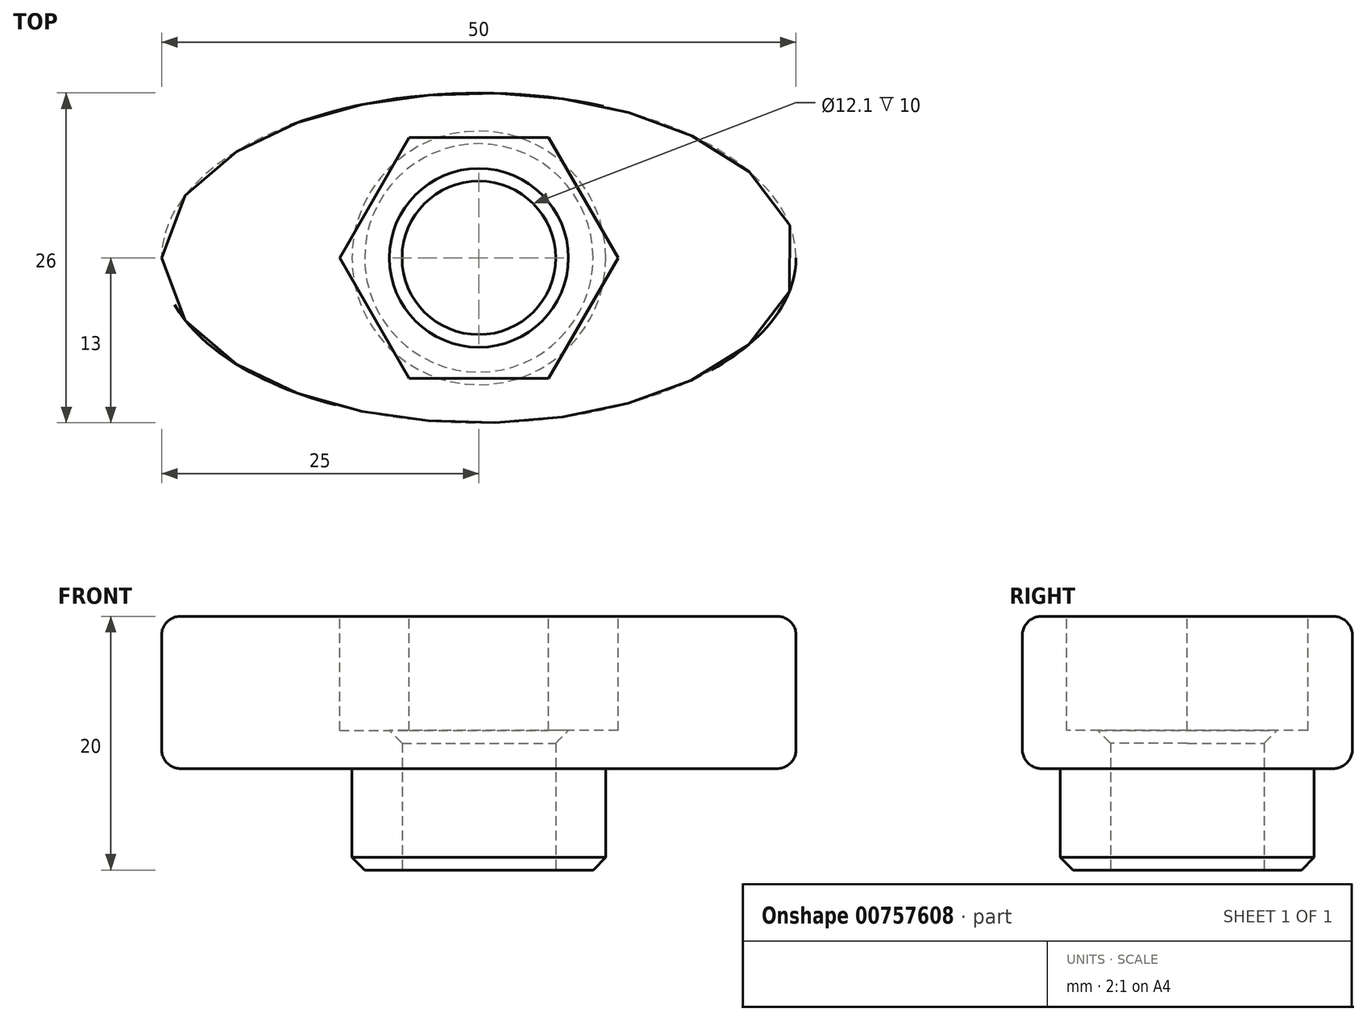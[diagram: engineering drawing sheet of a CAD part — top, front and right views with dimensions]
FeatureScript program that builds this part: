
annotation { "Feature Type Name" : "Feature", "Feature Type Description" : "" }
export const myFeature = defineFeature(function(context is Context, id is Id, definition is map)
    precondition{}
    {
        {
            var Q0;
            Q0=qCreatedBy(makeId("Top.planeOp"),FACE);
            var sketch = newSketch(context, id + "F0", { "sketchPlane" : qUnion([Q0])});
            skPoint(sketch, "E0", {"position": v(0, 13) * mm});
            skPoint(sketch, "E1", {"position": v(0, 0) * mm});
            skPoint(sketch, "E2", {"position": v(-25, 0) * mm});
            skEllipse(sketch, "E3", {"center": v(0, 0) * mm, "majorRadius": 25 * mm, "minorRadius": 13 * mm, "majorAxis": v(-1, 0)});
            skSolve(sketch);
        }
        {
            var Q0;
            Q0 = qSketchRegion(id + "F0", true);
            extrude(context, id + "F1", {"entities" : qUnion([Q0]), "depth" : 12 * mm, "offsetDistance" : 25 * mm});
        }
        {
            var Q0;
            Q0=makeQuery(id+"F1.opExtrude","CAP_FACE",FACE,{"disambiguationData":[OSD([sQuery(id+"F0.wireOp",EDGE,"E3")])],"isStart":true});
            var sketch = newSketch(context, id + "F2", { "sketchPlane" : qUnion([Q0])});
            skCircle(sketch, "E4", {"center": v(0, 0) * mm, "radius": 10 * mm});
            skSolve(sketch);
        }
        {
            var Q0;
            Q0 = qSketchRegion(id + "F2", true);
            extrude(context, id + "F3", {"entities" : qUnion([Q0]), "operationType" : NewBodyOperationType.ADD, "depth" : 8 * mm, "offsetDistance" : 25 * mm});
        }
        {
            var Q0;
            Q0=makeQuery(id+"F1.opExtrude","CAP_FACE",FACE,{"disambiguationData":[OSD([sQuery(id+"F0.wireOp",EDGE,"E3")])],"isStart":false});
            var sketch = newSketch(context, id + "F4", { "sketchPlane" : qUnion([Q0])});
            skCircle(sketch, "E5.cCircle", {"center": v(0, 0) * mm, "radius": 9.5 * mm, "construction": true});
            skLineSegment(sketch, "E5.0", {"start": v(10.97, 0) * mm, "end": v(5.48, -9.5) * mm});
            skLineSegment(sketch, "E5.1", {"start": v(5.48, -9.5) * mm, "end": v(-5.48, -9.5) * mm});
            skLineSegment(sketch, "E5.2", {"start": v(-5.48, -9.5) * mm, "end": v(-10.97, 0) * mm});
            skLineSegment(sketch, "E5.3", {"start": v(-10.97, 0) * mm, "end": v(-5.48, 9.5) * mm});
            skLineSegment(sketch, "E5.4", {"start": v(-5.48, 9.5) * mm, "end": v(5.48, 9.5) * mm});
            skLineSegment(sketch, "E5.5", {"start": v(5.48, 9.5) * mm, "end": v(10.97, 0) * mm});
            skPoint(sketch, "E5.0.midPoint", {"position": v(8.23, -4.75) * mm});
            skSolve(sketch);
        }
        {
            var Q0;
            Q0 = qSketchRegion(id + "F4", true);
            extrude(context, id + "F5", {"entities" : qUnion([Q0]), "operationType" : NewBodyOperationType.REMOVE, "oppositeDirection" : true, "depth" : 9 * mm, "offsetDistance" : 25 * mm});
        }
        {
            var Q0;
            Q0=makeQuery(id+"F3.opExtrude","CAP_FACE",FACE,{"disambiguationData":[OSD([sQuery(id+"F2.wireOp",EDGE,"E4")])],"isStart":false});
            var sketch = newSketch(context, id + "F6", { "sketchPlane" : qUnion([Q0])});
            skCircle(sketch, "E6", {"center": v(0, 0) * mm, "radius": 6.05 * mm});
            skSolve(sketch);
        }
        {
            var Q0;
            Q0 = qSketchRegion(id + "F6", true);
            extrude(context, id + "F7", {"entities" : qUnion([Q0]), "operationType" : NewBodyOperationType.REMOVE, "endBound" : BoundingType.THROUGH_ALL, "oppositeDirection" : true, "depth" : 25 * mm, "offsetDistance" : 25 * mm});
        }
        {
            var Q0;
            Q0=makeQuery(id+"F1.opExtrude","CAP_EDGE",EDGE,{"disambiguationData":[OSD([sQuery(id+"F0.wireOp",EDGE,"E3")])],"isStart":false});
            var Q1;
            Q1=makeQuery(id+"F1.opExtrude","CAP_EDGE",EDGE,{"disambiguationData":[OSD([sQuery(id+"F0.wireOp",EDGE,"E3")])],"isStart":true});
            var Q2;
            Q2=makeQuery(id+"F3.opExtrude","CAP_EDGE",EDGE,{"disambiguationData":[OSD([sQuery(id+"F2.wireOp",EDGE,"E4")])],"isStart":true});
            fillet(context, id + "F8", {"entities" : qUnion([Q0, Q1, Q2]), "radius" : 1.5 * mm, "tangentPropagation" : true, "allowEdgeOverflow" : false});
        }
        {
            var Q0;
            Q0=makeQuery(id+"F7.boolean.opBoolean","COPY",EDGE,{"derivedFrom":makeQuery(id+"F7.opExtrude","CAP_EDGE",EDGE,{"disambiguationData":[OSD([sQuery(id+"F6.wireOp",EDGE,"E6")])],"isStart":true})});
            var Q1;
            Q1=makeQuery(id+"F3.opExtrude","CAP_EDGE",EDGE,{"disambiguationData":[OSD([sQuery(id+"F2.wireOp",EDGE,"E4")])],"isStart":false});
            var Q2;
            Q2=makeQuery(id+"F5.boolean.opBoolean","COPY",EDGE,{"derivedFrom":makeQuery(id+"F5.opExtrude","CAP_EDGE",EDGE,{"disambiguationData":[OSD([sQuery(id+"F4.wireOp",EDGE,"E5.3")])],"isStart":true})});
            var Q3;
            Q3=makeQuery(id+"F5.boolean.opBoolean","COPY",EDGE,{"derivedFrom":makeQuery(id+"F5.opExtrude","CAP_EDGE",EDGE,{"disambiguationData":[OSD([sQuery(id+"F4.wireOp",EDGE,"E5.2")])],"isStart":true})});
            var Q4;
            Q4=makeQuery(id+"F5.boolean.opBoolean","COPY",EDGE,{"derivedFrom":makeQuery(id+"F5.opExtrude","CAP_EDGE",EDGE,{"disambiguationData":[OSD([sQuery(id+"F4.wireOp",EDGE,"E5.1")])],"isStart":true})});
            var Q5;
            Q5=makeQuery(id+"F5.boolean.opBoolean","COPY",EDGE,{"derivedFrom":makeQuery(id+"F5.opExtrude","CAP_EDGE",EDGE,{"disambiguationData":[OSD([sQuery(id+"F4.wireOp",EDGE,"E5.0")])],"isStart":true})});
            var Q6;
            Q6=makeQuery(id+"F5.boolean.opBoolean","COPY",EDGE,{"derivedFrom":makeQuery(id+"F5.opExtrude","CAP_EDGE",EDGE,{"disambiguationData":[OSD([sQuery(id+"F4.wireOp",EDGE,"E5.5")])],"isStart":true})});
            var Q7;
            Q7=makeQuery(id+"F5.boolean.opBoolean","COPY",EDGE,{"derivedFrom":makeQuery(id+"F5.opExtrude","CAP_EDGE",EDGE,{"disambiguationData":[OSD([sQuery(id+"F4.wireOp",EDGE,"E5.4")])],"isStart":true})});
            var Q8;
            Q8=makeQuery(id+"F7.boolean.opBoolean","INTERSECT",EDGE,{"derivedFrom":[makeQuery(id+"F5.boolean.opBoolean","COPY",FACE,{"derivedFrom":makeQuery(id+"F5.opExtrude","CAP_FACE",FACE,{"disambiguationData":[OSD([sQuery(id+"F4.wireOp",EDGE,"E5.0"),sQuery(id+"F4.wireOp",EDGE,"E5.1"),sQuery(id+"F4.wireOp",EDGE,"E5.2"),sQuery(id+"F4.wireOp",EDGE,"E5.3"),sQuery(id+"F4.wireOp",EDGE,"E5.4"),sQuery(id+"F4.wireOp",EDGE,"E5.5")])],"isStart":false})}),makeQuery(id+"F7.opExtrude","SWEPT_FACE",FACE,{"disambiguationData":[OSD([sQuery(id+"F6.wireOp",EDGE,"E6")])]})]});
            chamfer(context, id + "F9", {"entities" : qUnion([Q0, Q1, Q2, Q3, Q4, Q5, Q6, Q7, Q8]), "width" : 1 * mm, "tangentPropagation" : true});
        }
    });
